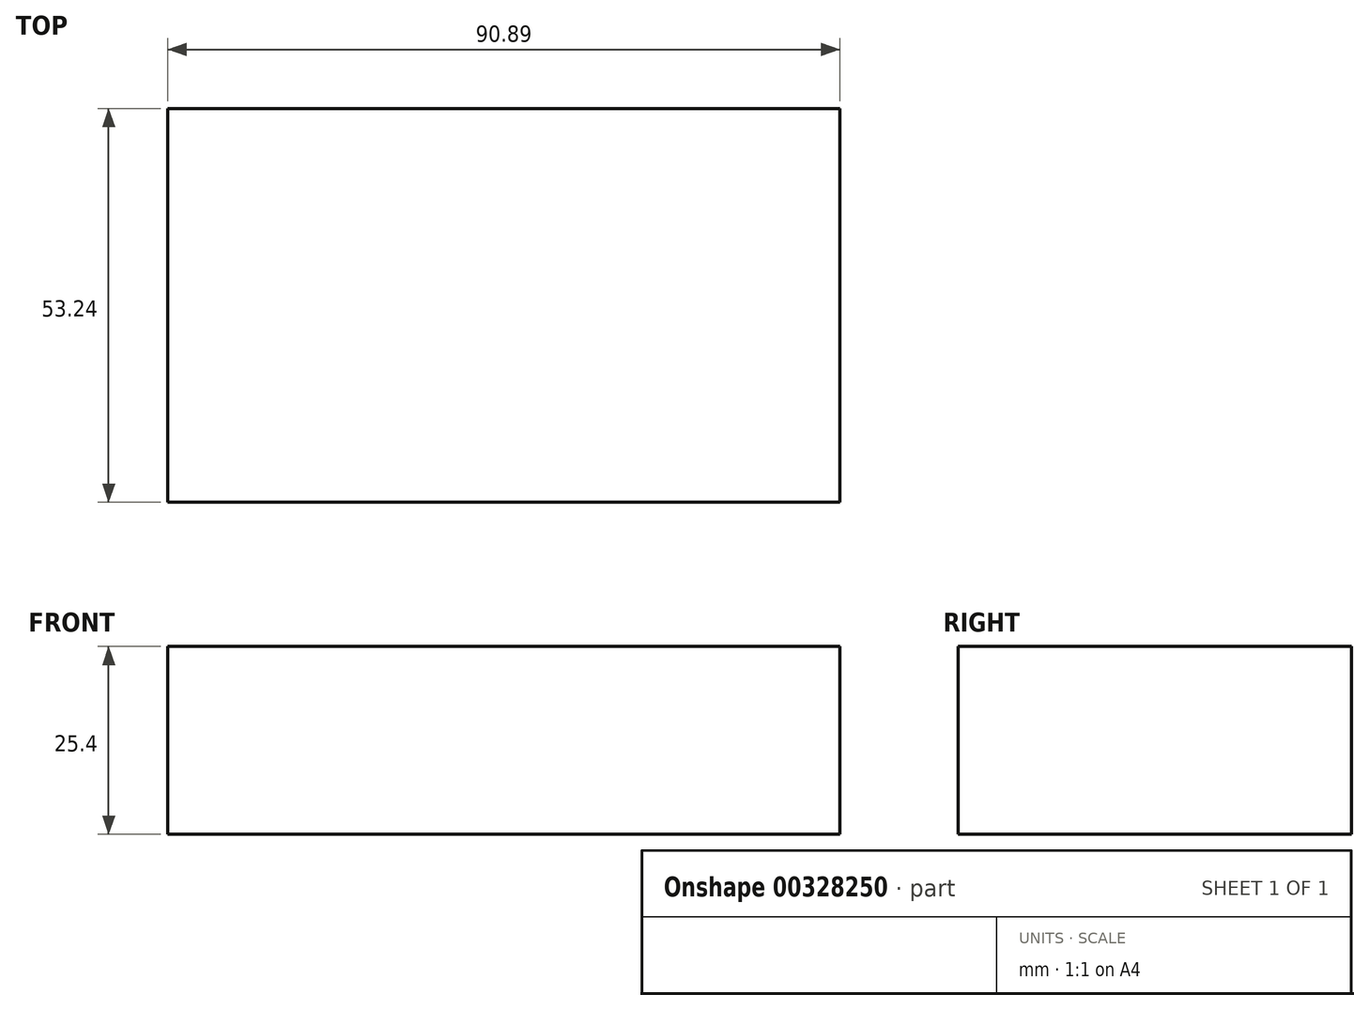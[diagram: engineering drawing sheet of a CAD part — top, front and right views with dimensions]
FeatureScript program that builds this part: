
annotation { "Feature Type Name" : "Feature", "Feature Type Description" : "" }
export const myFeature = defineFeature(function(context is Context, id is Id, definition is map)
    precondition{}
    {
        {
            var Q0;
            Q0=qCreatedBy(makeId("Top.planeOp"),FACE);
            var sketch = newSketch(context, id + "F0", { "sketchPlane" : qUnion([Q0])});
            skLineSegment(sketch, "E0.bottom", {"start": v(0, 0) * mm, "end": v(0, 0) * mm});
            skLineSegment(sketch, "E0.top", {"start": v(0, 0) * mm, "end": v(0, 0) * mm});
            skLineSegment(sketch, "E0.left", {"start": v(0, 0) * mm, "end": v(0, 0) * mm});
            skLineSegment(sketch, "E0.right", {"start": v(0, 0) * mm, "end": v(0, 0) * mm});
            skLineSegment(sketch, "E1.bottom", {"start": v(37.78, 18.63) * mm, "end": v(-53.11, 18.63) * mm});
            skLineSegment(sketch, "E1.top", {"start": v(37.78, -34.6) * mm, "end": v(-53.11, -34.6) * mm});
            skLineSegment(sketch, "E1.left", {"start": v(37.78, 18.63) * mm, "end": v(37.78, -34.6) * mm});
            skLineSegment(sketch, "E1.right", {"start": v(-53.11, 18.63) * mm, "end": v(-53.11, -34.6) * mm});
            skSolve(sketch);
        }
        {
            var Q0;
            Q0 = qSketchRegion(id + "F0", true);
            extrude(context, id + "F1", {"entities" : qUnion([Q0]), "depth" : 25.4 * mm});
        }
    });
